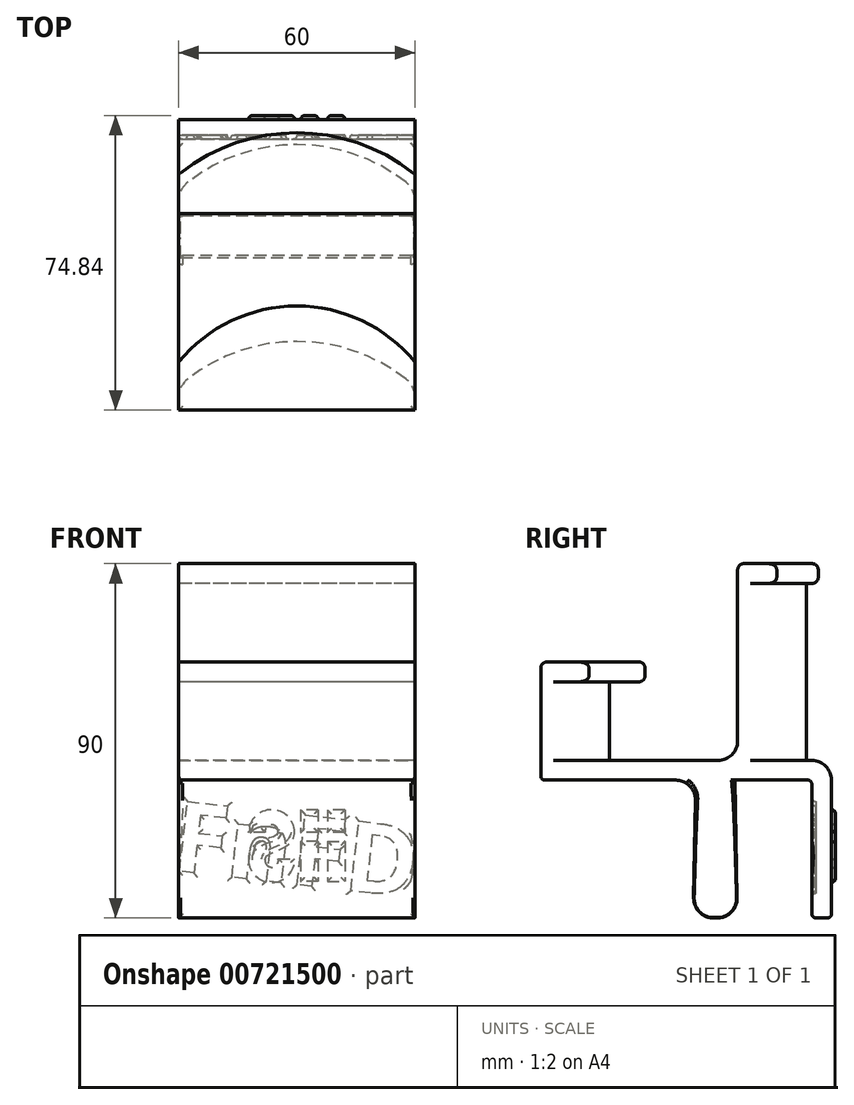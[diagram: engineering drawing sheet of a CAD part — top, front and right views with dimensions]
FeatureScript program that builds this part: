
annotation { "Feature Type Name" : "Feature", "Feature Type Description" : "" }
export const myFeature = defineFeature(function(context is Context, id is Id, definition is map)
    precondition{}
    {
        {
            var Q0;
            Q0=qCreatedBy(makeId("Top.planeOp"),FACE);
            var sketch = newSketch(context, id + "F0", { "sketchPlane" : qUnion([Q0])});
            skArc(sketch, "E0", {"start": v(27.7, 1.93) * mm, "mid": v(0, 11.46) * mm, "end": v(-27.7, 1.93) * mm});
            skLineSegment(sketch, "E1", {"start": v(0, 0) * mm, "end": v(0, -33.54) * mm, "construction": true});
            skLineSegment(sketch, "E2.bottom", {"start": v(-30, 0) * mm, "end": v(30, 0) * mm, "construction": true});
            skLineSegment(sketch, "E2.top", {"start": v(-30, -6) * mm, "end": v(30, -6) * mm});
            skLineSegment(sketch, "E2.left", {"start": v(-30, -2.8) * mm, "end": v(-30, -6) * mm});
            skLineSegment(sketch, "E2.right", {"start": v(30, -2.8) * mm, "end": v(30, -6) * mm});
            skPoint(sketch, "E3.visualSharp", {"position": v(30, 0) * mm});
            skArc(sketch, "E3.filletArc", {"start": v(30, -2.8) * mm, "mid": v(29.4, -0.17) * mm, "end": v(27.7, 1.93) * mm});
            skPoint(sketch, "E4.visualSharp", {"position": v(-30, 0) * mm});
            skArc(sketch, "E4.filletArc", {"start": v(-27.7, 1.93) * mm, "mid": v(-29.4, -0.17) * mm, "end": v(-30, -2.8) * mm});
            skSolve(sketch);
        }
        {
            var Q0;
            Q0=makeQuery(id+"F0.imprint","IMPRINT",FACE,{"disambiguationData":[TD([[makeQuery(id+"F0.imprint","IMPRINT",EDGE,{"derivedFrom":sQuery(id+"F0.wireOp",EDGE,"E0")}),1.0]])]});
            extrude(context, id + "F1", {"entities" : qUnion([Q0]), "depth" : 45 * mm, "offsetDistance" : 25 * mm});
        }
        {
            var Q0;
            Q0=makeQuery(id+"F1.opExtrude","CAP_FACE",FACE,{"disambiguationData":[OSD([sQuery(id+"F0.wireOp",EDGE,"E0"),sQuery(id+"F0.wireOp",EDGE,"E2.top"),sQuery(id+"F0.wireOp",EDGE,"E2.left"),sQuery(id+"F0.wireOp",EDGE,"E2.right"),sQuery(id+"F0.wireOp",EDGE,"E3.filletArc"),sQuery(id+"F0.wireOp",EDGE,"E4.filletArc")])],"isStart":false});
            var sketch = newSketch(context, id + "F2", { "sketchPlane" : qUnion([Q0])});
            skArc(sketch, "E5.0", {"start": v(33, -2.8) * mm, "mid": v(32.09, 1.15) * mm, "end": v(29.54, 4.3) * mm});
            skArc(sketch, "E5.1", {"start": v(-29.54, 4.3) * mm, "mid": v(-32.09, 1.15) * mm, "end": v(-33, -2.8) * mm});
            skLineSegment(sketch, "E5.2", {"start": v(-33, -2.8) * mm, "end": v(-33, -9) * mm});
            skArc(sketch, "E5.3", {"start": v(29.54, 4.3) * mm, "mid": v(0, 14.46) * mm, "end": v(-29.54, 4.3) * mm});
            skLineSegment(sketch, "E5.4", {"start": v(-33, -9) * mm, "end": v(33, -9) * mm});
            skLineSegment(sketch, "E5.5", {"start": v(33, -2.8) * mm, "end": v(33, -9) * mm});
            skLineSegment(sketch, "E6", {"start": v(-30, -6) * mm, "end": v(-33, -6) * mm});
            skPoint(sketch, "E6.endSnap0", {"position": v(-33, -5.9) * mm});
            skLineSegment(sketch, "E7", {"start": v(30, -6) * mm, "end": v(33, -6) * mm});
            skPoint(sketch, "E7.endSnap0", {"position": v(33, -5.9) * mm});
            skSolve(sketch);
        }
        {
            var Q0;
            Q0=makeQuery(id+"F2.imprint","IMPRINT",FACE,{"disambiguationData":[TD([[makeQuery(id+"F2.imprint","IMPRINT",EDGE,{"derivedFrom":sQuery(id+"F2.wireOp",EDGE,"E5.0")}),1.0]])]});
            var Q1;
            Q1=makeQuery(id+"F2.imprint","IMPRINT",FACE,{"disambiguationData":[TD([[makeQuery(id+"F2.imprint","IMPRINT",EDGE,{"derivedFrom":makeQuery(id+"F1.opExtrude","CAP_EDGE",EDGE,{"disambiguationData":[OSD([sQuery(id+"F0.wireOp",EDGE,"E0")])],"isStart":false})}),1.0]])]});
            extrude(context, id + "F3", {"entities" : qUnion([Q0, Q1]), "operationType" : NewBodyOperationType.ADD, "depth" : 5 * mm, "offsetDistance" : 25 * mm});
        }
        {
            var Q0;
            Q0=makeQuery(id+"F1.opExtrude","CAP_EDGE",EDGE,{"disambiguationData":[OSD([sQuery(id+"F0.wireOp",EDGE,"E0")])],"isStart":false});
            var Q1;
            Q1=makeQuery(id+"F3.opExtrude","CAP_EDGE",EDGE,{"disambiguationData":[OSD([sQuery(id+"F2.wireOp",EDGE,"E5.3")])],"isStart":true});
            var Q2;
            Q2=makeQuery(id+"F3.opExtrude","CAP_EDGE",EDGE,{"disambiguationData":[OSD([sQuery(id+"F2.wireOp",EDGE,"E5.3")])],"isStart":false});
            var Q3;
            Q3=makeQuery(id+"F1.opExtrude","CAP_EDGE",EDGE,{"disambiguationData":[OSD([sQuery(id+"F0.wireOp",EDGE,"E4.filletArc")])],"isStart":false});
            var Q4;
            Q4=makeQuery(id+"F3.opExtrude","CAP_EDGE",EDGE,{"disambiguationData":[OSD([sQuery(id+"F2.wireOp",EDGE,"E5.1")])],"isStart":true});
            var Q5;
            Q5=makeQuery(id+"F1.opExtrude","CAP_EDGE",EDGE,{"disambiguationData":[OSD([sQuery(id+"F0.wireOp",EDGE,"E2.left")])],"isStart":false});
            var Q6;
            Q6=makeQuery(id+"F3.opExtrude","CAP_EDGE",EDGE,{"disambiguationData":[OSD([sQuery(id+"F2.wireOp",EDGE,"E5.2")])],"isStart":true});
            var Q7;
            Q7=makeQuery(id+"F3.opExtrude","CAP_EDGE",EDGE,{"disambiguationData":[OSD([sQuery(id+"F2.wireOp",EDGE,"E5.1")])],"isStart":false});
            var Q8;
            Q8=makeQuery(id+"F3.opExtrude","CAP_EDGE",EDGE,{"disambiguationData":[OSD([sQuery(id+"F2.wireOp",EDGE,"E5.2")])],"isStart":false});
            var Q9;
            Q9=makeQuery(id+"F3.opExtrude","CAP_EDGE",EDGE,{"disambiguationData":[OSD([sQuery(id+"F2.wireOp",EDGE,"E5.0")])],"isStart":true});
            var Q10;
            Q10=makeQuery(id+"F3.opExtrude","CAP_EDGE",EDGE,{"disambiguationData":[OSD([sQuery(id+"F2.wireOp",EDGE,"E5.0")])],"isStart":false});
            var Q11;
            Q11=makeQuery(id+"F3.opExtrude","CAP_EDGE",EDGE,{"disambiguationData":[OSD([sQuery(id+"F2.wireOp",EDGE,"E5.5")])],"isStart":true});
            var Q12;
            Q12=makeQuery(id+"F3.opExtrude","CAP_EDGE",EDGE,{"disambiguationData":[OSD([sQuery(id+"F2.wireOp",EDGE,"E5.5")])],"isStart":false});
            var Q13;
            Q13=makeQuery(id+"F1.opExtrude","CAP_EDGE",EDGE,{"disambiguationData":[OSD([sQuery(id+"F0.wireOp",EDGE,"E3.filletArc")])],"isStart":false});
            var Q14;
            Q14=makeQuery(id+"F1.opExtrude","CAP_EDGE",EDGE,{"disambiguationData":[OSD([sQuery(id+"F0.wireOp",EDGE,"E2.right")])],"isStart":false});
            fillet(context, id + "F4", {"entities" : qUnion([Q0, Q1, Q2, Q3, Q4, Q5, Q6, Q7, Q8, Q9, Q10, Q11, Q12, Q13, Q14]), "radius" : 1.5 * mm, "tangentPropagation" : true, "allowEdgeOverflow" : false});
        }
        {
            var Q0;
            Q0=makeQuery(id+"F1.opExtrude","CAP_FACE",FACE,{"disambiguationData":[OSD([sQuery(id+"F0.wireOp",EDGE,"E0"),sQuery(id+"F0.wireOp",EDGE,"E2.top"),sQuery(id+"F0.wireOp",EDGE,"E2.left"),sQuery(id+"F0.wireOp",EDGE,"E2.right"),sQuery(id+"F0.wireOp",EDGE,"E3.filletArc"),sQuery(id+"F0.wireOp",EDGE,"E4.filletArc")])],"isStart":true});
            var sketch = newSketch(context, id + "F5", { "sketchPlane" : qUnion([Q0])});
            skLineSegment(sketch, "E8.bottom", {"start": v(-30, 6) * mm, "end": v(30, 6) * mm});
            skLineSegment(sketch, "E8.top", {"start": v(-30, -17.84) * mm, "end": v(30, -17.84) * mm});
            skLineSegment(sketch, "E8.left", {"start": v(-30, 6) * mm, "end": v(-30, -17.84) * mm});
            skLineSegment(sketch, "E8.right", {"start": v(30, 6) * mm, "end": v(30, -17.84) * mm});
            skLineSegment(sketch, "E9.bottom", {"start": v(-30, 6) * mm, "end": v(30, 6) * mm, "construction": true});
            skLineSegment(sketch, "E9.top", {"start": v(-30, 56) * mm, "end": v(30, 56) * mm});
            skLineSegment(sketch, "E9.left", {"start": v(-30, 6) * mm, "end": v(-30, 56) * mm});
            skLineSegment(sketch, "E9.right", {"start": v(30, 6) * mm, "end": v(30, 56) * mm});
            skSolve(sketch);
        }
        {
            var Q0;
            {var subQ2=sQuery(id+"F5.wireOp",EDGE,"E8.top");Q0=makeQuery(id+"F5.imprint","IMPRINT",FACE,{"disambiguationData":[TD([[makeQuery(id+"F5.imprint","IMPRINT",EDGE,{"derivedFrom":subQ2}),1.0]])]});}
            var Q1;
            {var subQ1=sQuery(id+"F5.wireOp",EDGE,"E8.bottom");Q1=makeQuery(id+"F5.imprint","IMPRINT",FACE,{"disambiguationData":[TD([[makeQuery(id+"F5.imprint","IMPRINT",EDGE,{"derivedFrom":subQ1}),-1.0]])]});}
            var Q2;
            Q2=makeQuery(id+"F5.imprint","IMPRINT",FACE,{"disambiguationData":[TD([[makeQuery(id+"F5.imprint","IMPRINT",EDGE,{"derivedFrom":sQuery(id+"F5.wireOp",EDGE,"E8.bottom")}),1.0]])]});
            extrude(context, id + "F6", {"entities" : qUnion([Q0, Q1, Q2]), "operationType" : NewBodyOperationType.ADD, "depth" : 5 * mm, "offsetDistance" : 25 * mm});
        }
        {
            var Q0;
            Q0=makeQuery(id+"F6.opExtrude","CAP_FACE",FACE,{"disambiguationData":[OSD([sQuery(id+"F5.wireOp",EDGE,"E8.top"),sQuery(id+"F5.wireOp",EDGE,"E8.left"),sQuery(id+"F5.wireOp",EDGE,"E8.right"),sQuery(id+"F5.wireOp",EDGE,"E9.top"),sQuery(id+"F5.wireOp",EDGE,"E9.left"),sQuery(id+"F5.wireOp",EDGE,"E9.right")])],"isStart":false});
            var sketch = newSketch(context, id + "F7", { "sketchPlane" : qUnion([Q0])});
            skLineSegment(sketch, "E10.bottom", {"start": v(-30, -17.84) * mm, "end": v(30, -17.84) * mm});
            skLineSegment(sketch, "E10.top", {"start": v(-30, -12.84) * mm, "end": v(30, -12.84) * mm});
            skLineSegment(sketch, "E10.left", {"start": v(-30, -17.84) * mm, "end": v(-30, -12.84) * mm});
            skLineSegment(sketch, "E10.right", {"start": v(30, -17.84) * mm, "end": v(30, -12.84) * mm});
            skSolve(sketch);
        }
        {
            var Q0;
            Q0=makeQuery(id+"F7.imprint","IMPRINT",FACE,{"disambiguationData":[TD([[makeQuery(id+"F7.imprint","IMPRINT",EDGE,{"derivedFrom":sQuery(id+"F7.wireOp",EDGE,"E10.bottom")}),1.0]])]});
            extrude(context, id + "F8", {"entities" : qUnion([Q0]), "operationType" : NewBodyOperationType.ADD, "depth" : 35 * mm, "offsetDistance" : 25 * mm});
        }
        {
            var Q0;
            Q0=makeQuery(id+"F8.opExtrude","CAP_FACE",FACE,{"disambiguationData":[OSD([sQuery(id+"F7.wireOp",EDGE,"E10.bottom"),sQuery(id+"F7.wireOp",EDGE,"E10.top"),sQuery(id+"F7.wireOp",EDGE,"E10.left"),sQuery(id+"F7.wireOp",EDGE,"E10.right")])],"isStart":false});
            var sketch = newSketch(context, id + "F9", { "sketchPlane" : qUnion([Q0])});
            skLineSegment(sketch, "E11.bottom", {"start": v(-30, -17.84) * mm, "end": v(30, -17.84) * mm});
            skLineSegment(sketch, "E11.top", {"start": v(-30, 12.16) * mm, "end": v(30, 12.16) * mm});
            skLineSegment(sketch, "E11.left", {"start": v(-30, -17.84) * mm, "end": v(-30, 12.16) * mm});
            skLineSegment(sketch, "E11.right", {"start": v(30, -17.84) * mm, "end": v(30, 12.16) * mm});
            skSolve(sketch);
        }
        {
            var Q0;
            Q0=makeQuery(id+"F8.opExtrude","CAP_EDGE",EDGE,{"disambiguationData":[OSD([sQuery(id+"F7.wireOp",EDGE,"E10.top")])],"isStart":true});
            var Q1;
            Q1=makeQuery(id+"F1.opExtrude","CAP_EDGE",EDGE,{"disambiguationData":[OSD([sQuery(id+"F0.wireOp",EDGE,"E2.top")])],"isStart":true});
            var Q2;
            Q2=makeQuery(id+"F6.opExtrude","CAP_EDGE",EDGE,{"disambiguationData":[OSD([sQuery(id+"F5.wireOp",EDGE,"E8.top")])],"isStart":true});
            fillet(context, id + "F10", {"entities" : qUnion([Q0, Q1, Q2]), "radius" : 5 * mm, "tangentPropagation" : true, "allowEdgeOverflow" : false});
        }
        {
            var Q0;
            Q0=makeQuery(id+"F8.opExtrude","SWEPT_FACE",FACE,{"disambiguationData":[OSD([sQuery(id+"F7.wireOp",EDGE,"E10.top")])]});
            var sketch = newSketch(context, id + "F11", { "sketchPlane" : qUnion([Q0])});
            skText(sketch, "E12", { "text": "FnFD", "fontName": "OpenSans-Bold.ttf"});
            const initialGuessF11  = {"E12": [-0.03206, -0.02786, 0.99344, -0.11434, 0.01798]};
            skSetInitialGuess(sketch, initialGuessF11);
            skSolve(sketch);
        }
        {
            var Q0;
            Q0=makeQuery(id+"F11.imprint","IMPRINT",FACE,{"disambiguationData":[TD([[makeQuery(id+"F11.imprint","IMPRINT",EDGE,{"derivedFrom":sQuery(id+"F11.wireOp",EDGE,"E12.sketch_text.stroke-0")}),-1.0]])]});
            var Q1;
            Q1=makeQuery(id+"F11.imprint","IMPRINT",FACE,{"disambiguationData":[TD([[makeQuery(id+"F11.imprint","IMPRINT",EDGE,{"derivedFrom":sQuery(id+"F11.wireOp",EDGE,"E12.sketch_text.stroke-10")}),-1.0]])]});
            var Q2;
            Q2=makeQuery(id+"F11.imprint","IMPRINT",FACE,{"disambiguationData":[TD([[makeQuery(id+"F11.imprint","IMPRINT",EDGE,{"derivedFrom":sQuery(id+"F11.wireOp",EDGE,"E12.sketch_text.stroke-27")}),-1.0]])]});
            var Q3;
            Q3=makeQuery(id+"F11.imprint","IMPRINT",FACE,{"disambiguationData":[TD([[makeQuery(id+"F11.imprint","IMPRINT",EDGE,{"derivedFrom":sQuery(id+"F11.wireOp",EDGE,"E12.sketch_text.stroke-37")}),-1.0]])]});
            var Q4;
            {var subQ6=sQuery(id+"F11.wireOp",EDGE,"E12.sketch_text.stroke-2");Q4=makeQuery(id+"F11.imprint","IMPRINT",FACE,{"disambiguationData":[TD([[makeQuery(id+"F11.imprint","IMPRINT",EDGE,{"derivedFrom":subQ6}),-1.0]])]});}
            extrude(context, id + "F12", {"entities" : qUnion([Q0, Q1, Q2, Q3, Q4]), "operationType" : NewBodyOperationType.REMOVE, "oppositeDirection" : true, "depth" : 1 * mm, "offsetDistance" : 25 * mm});
        }
        {
            var Q0;
            {var subQ0=sQuery(id+"F0.wireOp",EDGE,"E2.top");var subQ1=sQuery(id+"F5.wireOp",EDGE,"E9.top");var subQ2=sQuery(id+"F5.wireOp",EDGE,"E9.right");var subQ3=sQuery(id+"F5.wireOp",EDGE,"E8.right");var subQ4=sQuery(id+"F5.wireOp",EDGE,"E9.left");var subQ5=sQuery(id+"F5.wireOp",EDGE,"E8.left");Q0=makeQuery(id+"F6.boolean.opBoolean","SPLIT",FACE,{"disambiguationData":[TD([makeQuery(id+"F1.opExtrude","SWEPT_FACE",FACE,{"disambiguationData":[OSD([subQ0])]})])],"derivedFrom":makeQuery(id+"F6.opExtrude","CAP_FACE",FACE,{"disambiguationData":[OSD([sQuery(id+"F5.wireOp",EDGE,"E8.top"),subQ5,subQ3,subQ1,subQ4,subQ2])],"isStart":true})});}
            var sketch = newSketch(context, id + "F13", { "sketchPlane" : qUnion([Q0])});
            skArc(sketch, "E13", {"start": v(27.7, -48.07) * mm, "mid": v(0, -38.54) * mm, "end": v(-27.7, -48.07) * mm});
            skLineSegment(sketch, "E14", {"start": v(0, -38.54) * mm, "end": v(0, -83.54) * mm, "construction": true});
            skLineSegment(sketch, "E15.bottom", {"start": v(-30, -50) * mm, "end": v(30, -50) * mm, "construction": true});
            skLineSegment(sketch, "E15.top", {"start": v(-30, -56) * mm, "end": v(30, -56) * mm});
            skLineSegment(sketch, "E15.left", {"start": v(-30, -52.8) * mm, "end": v(-30, -56) * mm});
            skLineSegment(sketch, "E15.right", {"start": v(30, -52.8) * mm, "end": v(30, -56) * mm});
            skPoint(sketch, "E16.visualSharp", {"position": v(30, -50) * mm});
            skArc(sketch, "E16.filletArc", {"start": v(30, -52.8) * mm, "mid": v(29.4, -50.17) * mm, "end": v(27.7, -48.07) * mm});
            skPoint(sketch, "E17.visualSharp", {"position": v(-30, -50) * mm});
            skArc(sketch, "E17.filletArc", {"start": v(-27.7, -48.07) * mm, "mid": v(-29.4, -50.17) * mm, "end": v(-30, -52.8) * mm});
            skSolve(sketch);
        }
        {
            var Q0;
            Q0=makeQuery(id+"F13.imprint","IMPRINT",FACE,{"disambiguationData":[TD([[makeQuery(id+"F13.imprint","IMPRINT",EDGE,{"derivedFrom":sQuery(id+"F13.wireOp",EDGE,"E13")}),1.0]])]});
            extrude(context, id + "F14", {"entities" : qUnion([Q0]), "operationType" : NewBodyOperationType.ADD, "depth" : 20 * mm, "offsetDistance" : 25 * mm});
        }
        {
            var Q0;
            Q0=makeQuery(id+"F14.opExtrude","CAP_FACE",FACE,{"disambiguationData":[OSD([sQuery(id+"F13.wireOp",EDGE,"E13"),sQuery(id+"F13.wireOp",EDGE,"E15.top"),sQuery(id+"F13.wireOp",EDGE,"E15.left"),sQuery(id+"F13.wireOp",EDGE,"E15.right"),sQuery(id+"F13.wireOp",EDGE,"E16.filletArc"),sQuery(id+"F13.wireOp",EDGE,"E17.filletArc")])],"isStart":false});
            var sketch = newSketch(context, id + "F15", { "sketchPlane" : qUnion([Q0])});
            skLineSegment(sketch, "E18.2", {"start": v(-33, -48) * mm, "end": v(-33, -56) * mm});
            skLineSegment(sketch, "E18.4", {"start": v(-33, -56) * mm, "end": v(33, -56) * mm});
            skLineSegment(sketch, "E18.5", {"start": v(33, -48) * mm, "end": v(33, -56) * mm});
            skLineSegment(sketch, "E19", {"start": v(-30, -53) * mm, "end": v(-33, -53) * mm});
            skPoint(sketch, "E19.endSnap0", {"position": v(-33, -52) * mm});
            skLineSegment(sketch, "E20", {"start": v(30, -52.56) * mm, "end": v(33, -52.56) * mm});
            skPoint(sketch, "E20.endSnap0", {"position": v(33, -52) * mm});
            skLineSegment(sketch, "E21", {"start": v(0, -56) * mm, "end": v(0, -52.75) * mm, "construction": true});
            skLineSegment(sketch, "E22", {"start": v(0, -56) * mm, "end": v(0, -60.11) * mm, "construction": true});
            skArc(sketch, "E23", {"start": v(33, -48) * mm, "mid": v(0, -29.54) * mm, "end": v(-33, -48) * mm});
            skSolve(sketch);
        }
        {
            var Q0;
            {var subQ3=sQuery(id+"F15.wireOp",EDGE,"E18.0");Q0=makeQuery(id+"F15.imprint","IMPRINT",FACE,{"disambiguationData":[TD([[makeQuery(id+"F15.imprint","IMPRINT",EDGE,{"derivedFrom":subQ3}),1.0]])]});}
            var Q1;
            Q1=makeQuery(id+"F15.imprint","IMPRINT",FACE,{"disambiguationData":[TD([[makeQuery(id+"F15.imprint","IMPRINT",EDGE,{"derivedFrom":makeQuery(id+"F14.opExtrude","CAP_EDGE",EDGE,{"disambiguationData":[OSD([sQuery(id+"F13.wireOp",EDGE,"E13")])],"isStart":false})}),1.0]])]});
            var Q2;
            {var subQ3=sQuery(id+"F15.wireOp",EDGE,"E19");Q2=makeQuery(id+"F15.imprint","IMPRINT",FACE,{"disambiguationData":[TD([[makeQuery(id+"F15.imprint","IMPRINT",EDGE,{"derivedFrom":subQ3}),1.0]])]});}
            var Q3;
            {var subQ5=sQuery(id+"F15.wireOp",EDGE,"E20");Q3=makeQuery(id+"F15.imprint","IMPRINT",FACE,{"disambiguationData":[TD([[makeQuery(id+"F15.imprint","IMPRINT",EDGE,{"derivedFrom":subQ5}),-1.0]])]});}
            var Q4;
            {var subQ3=sQuery(id+"F15.wireOp",EDGE,"E19");Q4=makeQuery(id+"F15.imprint","IMPRINT",FACE,{"disambiguationData":[TD([[makeQuery(id+"F15.imprint","IMPRINT",EDGE,{"derivedFrom":subQ3}),-1.0]])]});}
            extrude(context, id + "F16", {"entities" : qUnion([Q0, Q1, Q2, Q3, Q4]), "operationType" : NewBodyOperationType.ADD, "depth" : 5 * mm, "offsetDistance" : 25 * mm});
        }
        {
            var Q0;
            Q0=makeQuery(id+"F6.opExtrude","CAP_FACE",FACE,{"disambiguationData":[OSD([sQuery(id+"F5.wireOp",EDGE,"E8.top"),sQuery(id+"F5.wireOp",EDGE,"E8.left"),sQuery(id+"F5.wireOp",EDGE,"E8.right"),sQuery(id+"F5.wireOp",EDGE,"E9.top"),sQuery(id+"F5.wireOp",EDGE,"E9.left"),sQuery(id+"F5.wireOp",EDGE,"E9.right")])],"isStart":false});
            var sketch = newSketch(context, id + "F17", { "sketchPlane" : qUnion([Q0])});
            skLineSegment(sketch, "E24.bottom", {"start": v(-30, 16.66) * mm, "end": v(30, 16.66) * mm});
            skLineSegment(sketch, "E24.top", {"start": v(-30, 6.66) * mm, "end": v(30, 6.66) * mm});
            skLineSegment(sketch, "E24.left", {"start": v(-30, 16.66) * mm, "end": v(-30, 6.66) * mm});
            skLineSegment(sketch, "E24.right", {"start": v(30, 16.66) * mm, "end": v(30, 6.66) * mm});
            skSolve(sketch);
        }
        {
            var Q0;
            Q0=makeQuery(id+"F17.imprint","IMPRINT",FACE,{"disambiguationData":[TD([[makeQuery(id+"F17.imprint","IMPRINT",EDGE,{"derivedFrom":sQuery(id+"F17.wireOp",EDGE,"E24.bottom")}),-1.0]])]});
            var Q1;
            Q1=makeQuery(id+"F8.opExtrude","CAP_FACE",FACE,{"disambiguationData":[OSD([sQuery(id+"F7.wireOp",EDGE,"E10.bottom"),sQuery(id+"F7.wireOp",EDGE,"E10.top"),sQuery(id+"F7.wireOp",EDGE,"E10.left"),sQuery(id+"F7.wireOp",EDGE,"E10.right")])],"isStart":false});
            extrude(context, id + "F18", {"entities" : qUnion([Q0]), "operationType" : NewBodyOperationType.ADD, "endBound" : BoundingType.UP_TO_SURFACE, "depth" : 25 * mm, "endBoundEntityFace" : qUnion([Q1]), "offsetDistance" : 25 * mm, "hasDraft" : true, "draftAngle" : 1 * degree});
        }
        {
            var Q0;
            Q0=makeQuery(id+"F18.opExtrude","CAP_EDGE",EDGE,{"disambiguationData":[OSD([sQuery(id+"F17.wireOp",EDGE,"E24.top")])],"isStart":true});
            var Q1;
            Q1=makeQuery(id+"F18.opExtrude","CAP_EDGE",EDGE,{"disambiguationData":[OSD([sQuery(id+"F17.wireOp",EDGE,"E24.bottom")])],"isStart":true});
            var Q2;
            Q2=makeQuery(id+"F18.opExtrude","CAP_EDGE",EDGE,{"disambiguationData":[OSD([sQuery(id+"F17.wireOp",EDGE,"E24.top")])],"isStart":false});
            var Q3;
            Q3=makeQuery(id+"F18.opExtrude","CAP_EDGE",EDGE,{"disambiguationData":[OSD([sQuery(id+"F17.wireOp",EDGE,"E24.bottom")])],"isStart":false});
            fillet(context, id + "F19", {"entities" : qUnion([Q0, Q1, Q2, Q3]), "radius" : 5 * mm, "tangentPropagation" : true, "allowEdgeOverflow" : false});
        }
        {
            var Q0;
            Q0=makeQuery(id+"F14.opExtrude","CAP_EDGE",EDGE,{"disambiguationData":[OSD([sQuery(id+"F13.wireOp",EDGE,"E13")])],"isStart":true});
            var Q1;
            Q1=makeQuery(id+"F16.opExtrude","CAP_EDGE",EDGE,{"disambiguationData":[OSD([sQuery(id+"F15.wireOp",EDGE,"E18.3")])],"isStart":false});
            var Q2;
            Q2=makeQuery(id+"F16.opExtrude","CAP_EDGE",EDGE,{"disambiguationData":[OSD([sQuery(id+"F15.wireOp",EDGE,"E18.3")])],"isStart":true});
            var Q3;
            Q3=makeQuery(id+"F1.opExtrude","CAP_EDGE",EDGE,{"disambiguationData":[OSD([sQuery(id+"F0.wireOp",EDGE,"E0")])],"isStart":true});
            var Q4;
            Q4=makeQuery(id+"F14.opExtrude","CAP_EDGE",EDGE,{"disambiguationData":[OSD([sQuery(id+"F13.wireOp",EDGE,"E13")])],"isStart":false});
            var Q5;
            Q5=makeQuery(id+"F3.opExtrude","CAP_EDGE",EDGE,{"disambiguationData":[OSD([sQuery(id+"F0.wireOp",EDGE,"E2.top"),sQuery(id+"F2.wireOp",EDGE,"E6"),sQuery(id+"F2.wireOp",EDGE,"E7")])],"isStart":false});
            var Q6;
            Q6=makeQuery(id+"F16.opExtrude","CAP_EDGE",EDGE,{"disambiguationData":[OSD([sQuery(id+"F15.wireOp",EDGE,"E18.4")])],"isStart":false});
            var Q7;
            Q7=makeQuery(id+"F16.opExtrude","CAP_EDGE",EDGE,{"disambiguationData":[OSD([sQuery(id+"F15.wireOp",EDGE,"E23")])],"isStart":true});
            var Q8;
            Q8=makeQuery(id+"F16.opExtrude","CAP_EDGE",EDGE,{"disambiguationData":[OSD([sQuery(id+"F15.wireOp",EDGE,"E23")])],"isStart":false});
            fillet(context, id + "F20", {"entities" : qUnion([Q0, Q1, Q2, Q3, Q4, Q5, Q6, Q7, Q8]), "radius" : 1.5 * mm, "tangentPropagation" : true, "allowEdgeOverflow" : false});
        }
        {
            var Q0;
            {var subQ0=sQuery(id+"F7.wireOp",EDGE,"E10.top");Q0=makeQuery(id+"F12.boolean.opBoolean","SPLIT",FACE,{"disambiguationData":[TD([makeQuery(id+"F1.opExtrude","SWEPT_FACE",FACE,{"disambiguationData":[OSD([sQuery(id+"F0.wireOp",EDGE,"E2.left")])]})])],"derivedFrom":makeQuery(id+"F8.opExtrude","SWEPT_FACE",FACE,{"disambiguationData":[OSD([subQ0])]})});}
            var Q1;
            Q1=makeQuery(id+"F6.opExtrude","CAP_EDGE",EDGE,{"disambiguationData":[OSD([sQuery(id+"F5.wireOp",EDGE,"E9.top")])],"isStart":true});
            var Q2;
            Q2=makeQuery(id+"F6.opExtrude","CAP_EDGE",EDGE,{"disambiguationData":[OSD([sQuery(id+"F5.wireOp",EDGE,"E9.top")])],"isStart":false});
            var Q3;
            {var subQ0=sQuery(id+"F5.wireOp",EDGE,"E9.top");var subQ1=sQuery(id+"F5.wireOp",EDGE,"E9.left");var subQ2=sQuery(id+"F5.wireOp",EDGE,"E8.left");Q3=makeQuery(id+"F18.boolean.opBoolean","SPLIT",EDGE,{"disambiguationData":[TD([makeQuery(id+"F6.opExtrude","SWEPT_FACE",FACE,{"disambiguationData":[OSD([subQ0])]})])],"derivedFrom":makeQuery(id+"F6.opExtrude","CAP_EDGE",EDGE,{"disambiguationData":[OSD([subQ2,subQ1])],"isStart":false})});}
            var Q4;
            Q4=makeQuery(id+"F18.opExtrude","SWEPT_EDGE",EDGE,{"disambiguationData":[OSD([sQuery(id+"F5.wireOp",EDGE,"E8.left"),sQuery(id+"F5.wireOp",EDGE,"E9.left"),sQuery(id+"F17.wireOp",EDGE,"E24.bottom"),sQuery(id+"F17.wireOp",EDGE,"E24.left")])]});
            var Q5;
            Q5=makeQuery(id+"F18.opExtrude","SWEPT_EDGE",EDGE,{"disambiguationData":[OSD([sQuery(id+"F5.wireOp",EDGE,"E8.left"),sQuery(id+"F5.wireOp",EDGE,"E9.left"),sQuery(id+"F17.wireOp",EDGE,"E24.top"),sQuery(id+"F17.wireOp",EDGE,"E24.left")])]});
            var Q6;
            Q6=makeQuery(id+"F18.opExtrude","SWEPT_EDGE",EDGE,{"disambiguationData":[OSD([sQuery(id+"F5.wireOp",EDGE,"E8.right"),sQuery(id+"F5.wireOp",EDGE,"E9.right"),sQuery(id+"F17.wireOp",EDGE,"E24.top"),sQuery(id+"F17.wireOp",EDGE,"E24.right")])]});
            var Q7;
            Q7=makeQuery(id+"F18.opExtrude","SWEPT_EDGE",EDGE,{"disambiguationData":[OSD([sQuery(id+"F5.wireOp",EDGE,"E8.right"),sQuery(id+"F5.wireOp",EDGE,"E9.right"),sQuery(id+"F17.wireOp",EDGE,"E24.bottom"),sQuery(id+"F17.wireOp",EDGE,"E24.right")])]});
            var Q8;
            {var subQ0=sQuery(id+"F5.wireOp",EDGE,"E9.top");var subQ1=sQuery(id+"F5.wireOp",EDGE,"E9.right");var subQ2=sQuery(id+"F5.wireOp",EDGE,"E8.right");Q8=makeQuery(id+"F18.boolean.opBoolean","SPLIT",EDGE,{"disambiguationData":[TD([makeQuery(id+"F6.opExtrude","SWEPT_FACE",FACE,{"disambiguationData":[OSD([subQ0])]})])],"derivedFrom":makeQuery(id+"F6.opExtrude","CAP_EDGE",EDGE,{"disambiguationData":[OSD([subQ2,subQ1])],"isStart":false})});}
            var Q9;
            Q9=makeQuery(id+"F8.opExtrude","CAP_EDGE",EDGE,{"disambiguationData":[OSD([sQuery(id+"F7.wireOp",EDGE,"E10.bottom")])],"isStart":false});
            fillet(context, id + "F21", {"entities" : qUnion([Q0, Q1, Q2, Q3, Q4, Q5, Q6, Q7, Q8, Q9]), "radius" : 1 * mm, "tangentPropagation" : true, "allowEdgeOverflow" : false});
        }
        {
            var Q0;
            {var subQ0=sQuery(id+"F9.wireOp",EDGE,"E11.bottom");Q0=makeQuery(id+"F9.imprint","IMPRINT",FACE,{"disambiguationData":[TD([[makeQuery(id+"F9.imprint","IMPRINT",EDGE,{"derivedFrom":subQ0}),1.0]])]});}
            var sketch = newSketch(context, id + "F22", { "sketchPlane" : qUnion([Q0])});
            skLineSegment(sketch, "E25.top", {"start": v(-30, -18.33) * mm, "end": v(30, -18.33) * mm});
            skLineSegment(sketch, "E25.left", {"start": v(-30, 31.6) * mm, "end": v(-30, -18.33) * mm});
            skLineSegment(sketch, "E25.right", {"start": v(30, 31.6) * mm, "end": v(30, -18.33) * mm});
            skLineSegment(sketch, "E26.0", {"start": v(-35, 87.47) * mm, "end": v(-35, -23.33) * mm});
            skLineSegment(sketch, "E26.1", {"start": v(-35, 87.47) * mm, "end": v(35, 87.47) * mm});
            skLineSegment(sketch, "E26.2", {"start": v(35, 87.47) * mm, "end": v(35, -23.33) * mm});
            skLineSegment(sketch, "E26.3", {"start": v(-35, -23.33) * mm, "end": v(35, -23.33) * mm});
            skLineSegment(sketch, "E27", {"start": v(-30, 31.6) * mm, "end": v(-30, 60.9) * mm});
            skLineSegment(sketch, "E28", {"start": v(-30, 60.9) * mm, "end": v(30, 60.9) * mm});
            skLineSegment(sketch, "E29", {"start": v(30, 60.9) * mm, "end": v(30, 31.6) * mm});
            skSolve(sketch);
        }
        {
            var Q0;
            {var subQ0=sQuery(id+"F9.wireOp",EDGE,"E11.top");Q0=makeQuery(id+"F9.imprint","IMPRINT",FACE,{"disambiguationData":[TD([[makeQuery(id+"F9.imprint","IMPRINT",EDGE,{"derivedFrom":subQ0}),-1.0]])]});}
            var Q1;
            {var subQ0=sQuery(id+"F9.wireOp",EDGE,"E11.bottom");Q1=makeQuery(id+"F9.imprint","IMPRINT",FACE,{"disambiguationData":[TD([[makeQuery(id+"F9.imprint","IMPRINT",EDGE,{"derivedFrom":subQ0}),1.0]])]});}
            var Q2;
            {var subQ2=sQuery(id+"F22.wireOp",EDGE,"E27");Q2=makeQuery(id+"F22.imprint","IMPRINT",FACE,{"disambiguationData":[TD([[makeQuery(id+"F22.imprint","IMPRINT",EDGE,{"derivedFrom":subQ2}),-1.0]])]});}
            var Q3;
            {var subQ0=sQuery(id+"F22.wireOp",EDGE,"E25.top");Q3=makeQuery(id+"F22.imprint","IMPRINT",FACE,{"disambiguationData":[TD([[makeQuery(id+"F22.imprint","IMPRINT",EDGE,{"derivedFrom":subQ0}),1.0]])]});}
            extrude(context, id + "F23", {"entities" : qUnion([Q0, Q1, Q2, Q3]), "operationType" : NewBodyOperationType.INTERSECT, "oppositeDirection" : true, "depth" : 126.3 * mm, "offsetDistance" : 25 * mm});
        }
        {
            var Q0;
            Q0=makeQuery(id+"FKfYyVdWjElvuKf_1.boolean.opBoolean","MERGE",FACE,{"derivedFrom":[makeQuery(id+"F8.boolean.opBoolean","MERGE",FACE,{"derivedFrom":[makeQuery(id+"F6.opExtrude","SWEPT_FACE",FACE,{"disambiguationData":[OSD([sQuery(id+"F5.wireOp",EDGE,"E8.top")])]}),makeQuery(id+"F8.opExtrude","SWEPT_FACE",FACE,{"disambiguationData":[OSD([sQuery(id+"F7.wireOp",EDGE,"E10.bottom")])]})]}),makeQuery(id+"FKfYyVdWjElvuKf_1.opExtrude","SWEPT_FACE",FACE,{"disambiguationData":[OSD([sQuery(id+"F9.wireOp",EDGE,"E11.bottom")])]})]});
            var sketch = newSketch(context, id + "F24", { "sketchPlane" : qUnion([Q0])});
            skLineSegment(sketch, "E30.bottom", {"start": v(-12.2, -12.54) * mm, "end": v(-7.75, -12.54) * mm});
            skLineSegment(sketch, "E30.top", {"start": v(-12.2, -18.28) * mm, "end": v(-7.75, -18.28) * mm});
            skLineSegment(sketch, "E30.left", {"start": v(-12.2, -12.54) * mm, "end": v(-12.2, -18.28) * mm});
            skLineSegment(sketch, "E30.right", {"start": v(-7.75, -12.54) * mm, "end": v(-7.75, -18.28) * mm});
            skLineSegment(sketch, "E31.bottom", {"start": v(-7.78, -20.53) * mm, "end": v(-12.24, -20.53) * mm});
            skLineSegment(sketch, "E31.top", {"start": v(-7.78, -30.72) * mm, "end": v(-12.24, -30.72) * mm});
            skLineSegment(sketch, "E31.left", {"start": v(-7.78, -20.53) * mm, "end": v(-7.78, -30.72) * mm});
            skLineSegment(sketch, "E31.right", {"start": v(-12.24, -20.53) * mm, "end": v(-12.24, -30.72) * mm});
            skLineSegment(sketch, "E32.bottom", {"start": v(-5.44, -12.54) * mm, "end": v(-0.98, -12.54) * mm});
            skLineSegment(sketch, "E32.top", {"start": v(-5.44, -18.28) * mm, "end": v(-0.98, -18.28) * mm});
            skLineSegment(sketch, "E32.left", {"start": v(-5.44, -12.54) * mm, "end": v(-5.44, -18.28) * mm});
            skLineSegment(sketch, "E32.right", {"start": v(-0.98, -12.54) * mm, "end": v(-0.98, -18.28) * mm});
            skLineSegment(sketch, "E33.bottom", {"start": v(-5.44, -20.53) * mm, "end": v(-0.98, -20.53) * mm});
            skLineSegment(sketch, "E33.top", {"start": v(-5.44, -30.72) * mm, "end": v(-0.98, -30.72) * mm});
            skLineSegment(sketch, "E33.left", {"start": v(-5.44, -20.53) * mm, "end": v(-5.44, -30.72) * mm});
            skLineSegment(sketch, "E33.right", {"start": v(-0.98, -20.53) * mm, "end": v(-0.98, -30.72) * mm});
            skArc(sketch, "E34", {"start": v(12.28, -18.23) * mm, "mid": v(6.4, -12.5) * mm, "end": v(0.54, -18.23) * mm});
            skArc(sketch, "E35", {"start": v(0.54, -24.96) * mm, "mid": v(6.25, -30.98) * mm, "end": v(12.28, -25.27) * mm});
            skArc(sketch, "E36", {"start": v(8.05, -18.23) * mm, "mid": v(6.4, -16.37) * mm, "end": v(4.75, -18.23) * mm});
            skArc(sketch, "E37", {"start": v(4.75, -24.96) * mm, "mid": v(6.21, -27.11) * mm, "end": v(8.05, -25.27) * mm});
            skFitSpline(sketch, "E38", {"points": [v(8.05, -25.27) * mm, v(7.59, -24.2) * mm, v(6, -23.29) * mm, v(3.2, -22.02) * mm, v(1.42, -20.61) * mm, v(0.54, -18.23) * mm], "startDerivative": vector(-1.03, 10.2) * mm, "endDerivative": vector(0.23, 9.56) * mm});
            skFitSpline(sketch, "E39", {"points": [v(4.75, -18.23) * mm, v(5.4, -19.1) * mm, v(7.25, -19.8) * mm, v(8.96, -20.56) * mm, v(11.06, -21.9) * mm, v(12.01, -23.25) * mm, v(12.23, -24.39) * mm, v(12.28, -25.27) * mm], "startDerivative": vector(3.8, -8.54) * mm, "endDerivative": vector(-0.25, -8.28) * mm});
            skLineSegment(sketch, "E40", {"start": v(8.05, -18.23) * mm, "end": v(12.28, -18.23) * mm});
            skLineSegment(sketch, "E41", {"start": v(4.75, -24.96) * mm, "end": v(0.54, -24.96) * mm});
            skLineSegment(sketch, "E42.filletArc", {"start": v(0.54, -18.23) * mm, "end": v(0.54, -18.23) * mm});
            skSolve(sketch);
        }
        {
            var Q0;
            Q0=makeQuery(id+"F24.imprint","IMPRINT",FACE,{"disambiguationData":[TD([[makeQuery(id+"F24.imprint","IMPRINT",EDGE,{"derivedFrom":sQuery(id+"F24.wireOp",EDGE,"E30.bottom")}),-1.0]])]});
            var Q1;
            Q1=makeQuery(id+"F24.imprint","IMPRINT",FACE,{"disambiguationData":[TD([[makeQuery(id+"F24.imprint","IMPRINT",EDGE,{"derivedFrom":sQuery(id+"F24.wireOp",EDGE,"E32.bottom")}),-1.0]])]});
            var Q2;
            Q2=makeQuery(id+"F24.imprint","IMPRINT",FACE,{"disambiguationData":[TD([[makeQuery(id+"F24.imprint","IMPRINT",EDGE,{"derivedFrom":sQuery(id+"F24.wireOp",EDGE,"E31.bottom")}),1.0]])]});
            var Q3;
            Q3=makeQuery(id+"F24.imprint","IMPRINT",FACE,{"disambiguationData":[TD([[makeQuery(id+"F24.imprint","IMPRINT",EDGE,{"derivedFrom":sQuery(id+"F24.wireOp",EDGE,"E33.bottom")}),-1.0]])]});
            var Q4;
            Q4=makeQuery(id+"F24.imprint","IMPRINT",FACE,{"disambiguationData":[TD([[makeQuery(id+"F24.imprint","IMPRINT",EDGE,{"derivedFrom":sQuery(id+"F24.wireOp",EDGE,"E34")}),1.0]])]});
            extrude(context, id + "F25", {"entities" : qUnion([Q0, Q1, Q2, Q3, Q4]), "operationType" : NewBodyOperationType.ADD, "depth" : 1 * mm, "offsetDistance" : 25 * mm});
        }
        {
            var Q0;
            Q0=makeQuery(id+"F25.opExtrude","CAP_FACE",FACE,{"disambiguationData":[OSD([sQuery(id+"F24.wireOp",EDGE,"E32.bottom"),sQuery(id+"F24.wireOp",EDGE,"E32.top"),sQuery(id+"F24.wireOp",EDGE,"E32.left"),sQuery(id+"F24.wireOp",EDGE,"E32.right")])],"isStart":false});
            var Q1;
            Q1=makeQuery(id+"F25.opExtrude","CAP_FACE",FACE,{"disambiguationData":[OSD([sQuery(id+"F24.wireOp",EDGE,"E31.bottom"),sQuery(id+"F24.wireOp",EDGE,"E31.top"),sQuery(id+"F24.wireOp",EDGE,"E31.left"),sQuery(id+"F24.wireOp",EDGE,"E31.right")])],"isStart":false});
            var Q2;
            Q2=makeQuery(id+"F25.opExtrude","CAP_FACE",FACE,{"disambiguationData":[OSD([sQuery(id+"F24.wireOp",EDGE,"E33.bottom"),sQuery(id+"F24.wireOp",EDGE,"E33.top"),sQuery(id+"F24.wireOp",EDGE,"E33.left"),sQuery(id+"F24.wireOp",EDGE,"E33.right")])],"isStart":false});
            var Q3;
            Q3=makeQuery(id+"F25.opExtrude","CAP_EDGE",EDGE,{"disambiguationData":[OSD([sQuery(id+"F24.wireOp",EDGE,"E30.bottom")])],"isStart":false});
            var Q4;
            Q4=makeQuery(id+"F25.opExtrude","CAP_FACE",FACE,{"disambiguationData":[OSD([sQuery(id+"F24.wireOp",EDGE,"E30.bottom"),sQuery(id+"F24.wireOp",EDGE,"E30.top"),sQuery(id+"F24.wireOp",EDGE,"E30.left"),sQuery(id+"F24.wireOp",EDGE,"E30.right")])],"isStart":false});
            var Q5;
            Q5=makeQuery(id+"F25.opExtrude","CAP_FACE",FACE,{"disambiguationData":[OSD([sQuery(id+"F24.wireOp",EDGE,"E34"),sQuery(id+"F24.wireOp",EDGE,"E35"),sQuery(id+"F24.wireOp",EDGE,"E36"),sQuery(id+"F24.wireOp",EDGE,"E37"),sQuery(id+"F24.wireOp",EDGE,"E38"),sQuery(id+"F24.wireOp",EDGE,"E39"),sQuery(id+"F24.wireOp",EDGE,"E40"),sQuery(id+"F24.wireOp",EDGE,"E41")])],"isStart":false});
            fillet(context, id + "F26", {"entities" : qUnion([Q0, Q1, Q2, Q3, Q4, Q5]), "radius" : 1 * mm, "tangentPropagation" : true, "allowEdgeOverflow" : false});
        }
    });
